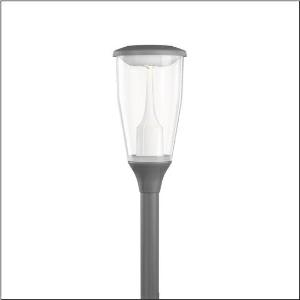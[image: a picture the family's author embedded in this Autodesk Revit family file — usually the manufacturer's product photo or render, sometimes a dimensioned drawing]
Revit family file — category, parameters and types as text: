
# Revit family: dl_11_iq___st1_2a_5xa5575af14hp00022_5e00
name_source: partatom
category: Lighting Fixtures
units: mm (PartAtom-declared; Revit-internal decimal feet)

## family parameters
Cut with Voids When Loaded = No
Host = Face
Light Source = No
Part Type = Normal
Room Calculation Point = No
Round Connector Dimension = Use Diameter
Shared = No

## types (1)
- --- (1 x LED, 4000 lm, 33.6 W, 2200K)
    Apparent Load = 34 VA
    CIE Flux Codes = 23 60 93 95 100
    Color Rendering = 70
    Color Temperature = 2200K
    Default Elevation = 1800 mm
    Description = DL 11 iQ, mast luminaire, Module 540 iQ-SR, primary light control with 3 zone facetted reflector, of plastic, silver coated, highly specular, structured, primary optical cover: cover, of PMMA, transparent, light distribution: ST1.2a, light emission: direct distribution, primary light characteristic: asymmetric, installation type: post-top, LED, High Power LED, rated luminous flux: 4.000lm, luminous efficacy: 119lm/W, light colour: 722, colour temperature: 2200K, control: Street-Remote, Auto-Match, Temp-Guard, Lumen-Switch, Night-Set, Smart-Wire, Light-Fading, Desk-Remote (wireless, voltage-free reading and setting of iQ features in the workshop via application-optimized NFC function/RFID function), optimised constant luminous flux control (CLO 2.0), mains connection: 220..240V, AC, 50/60Hz, connection cable pre-assembled, cable length: 5,5m, start of lifetime: 34W, end of service life: 36W, reduction: 15W, luminaire housing, upper part, of diecast aluminium, coated, Siteco® metallic grey (DB 702S), spigot size: 76mm (post-top), post-top mast mounting element, of diecast aluminium, coated, Siteco® metallic grey (DB 702S), Module 540 iQ-SR, traffic white (RAL 9016), equipment: Power, protection rating (complete): IP66, insulation class (complete): insulation class II (safety insulation), certification: CE, ENEC, ENEC+, VDE, packaging unit: 1 piece

Light Distribution: ST1.2a
    Height = 665 mm
    Lamp = 1 x LED
    Lamp Light Flux = 4000 lm
    Lamp Power = 33.6 W
    Lamp count = 1
    Length = 334 mm
    Luminous efficacy = 119 lm/W
    Manufacturer = Siteco
    ModVariant = No
    Model = 5XA5575AF14HP00022
    Number of Poles = 1
    OnlyDefault = Yes
    Power Factor = 1
    Product Name = DL 11 iQ | ST1.2a
    Product group = mast luminaire | pylon top
    ProductGroupID = 6100
    Protection Class = Protection class II
    Protection Degree = IP 66
    RLX_Detail_Level = 1
    RLX_Emergency_Light_Flux = 0 lm
    RLX_Emergency_Type = 0
    RLX_Emergency_Type_DB = No
    RlxData = <blob elided: 155361 chars, md5=16d923d7>
    Socket = socket
    Standby Power = 0 W
    System Light Flux = 4000 lm
    System Power = 34 W
    Type Comments = factory setting: luminous flux: 100 % | dim-lin: 254 | 695 mA
    Type Image = l_1258354.jpg
    URL = http://relux.com
    VarID = @adj_002003
    Voltage = 0 V
    Weight = 0.00 kg
    Width = 0 mm  [stored 0 ft]

note: [stored X ft] marks values corroborated as IEEE doubles in the binary element streams (Revit-internal decimal feet)

## geometry (parser evidence)
native form markers: Blend x4, Sweep x12
no freeform markers — native parametric forms only
